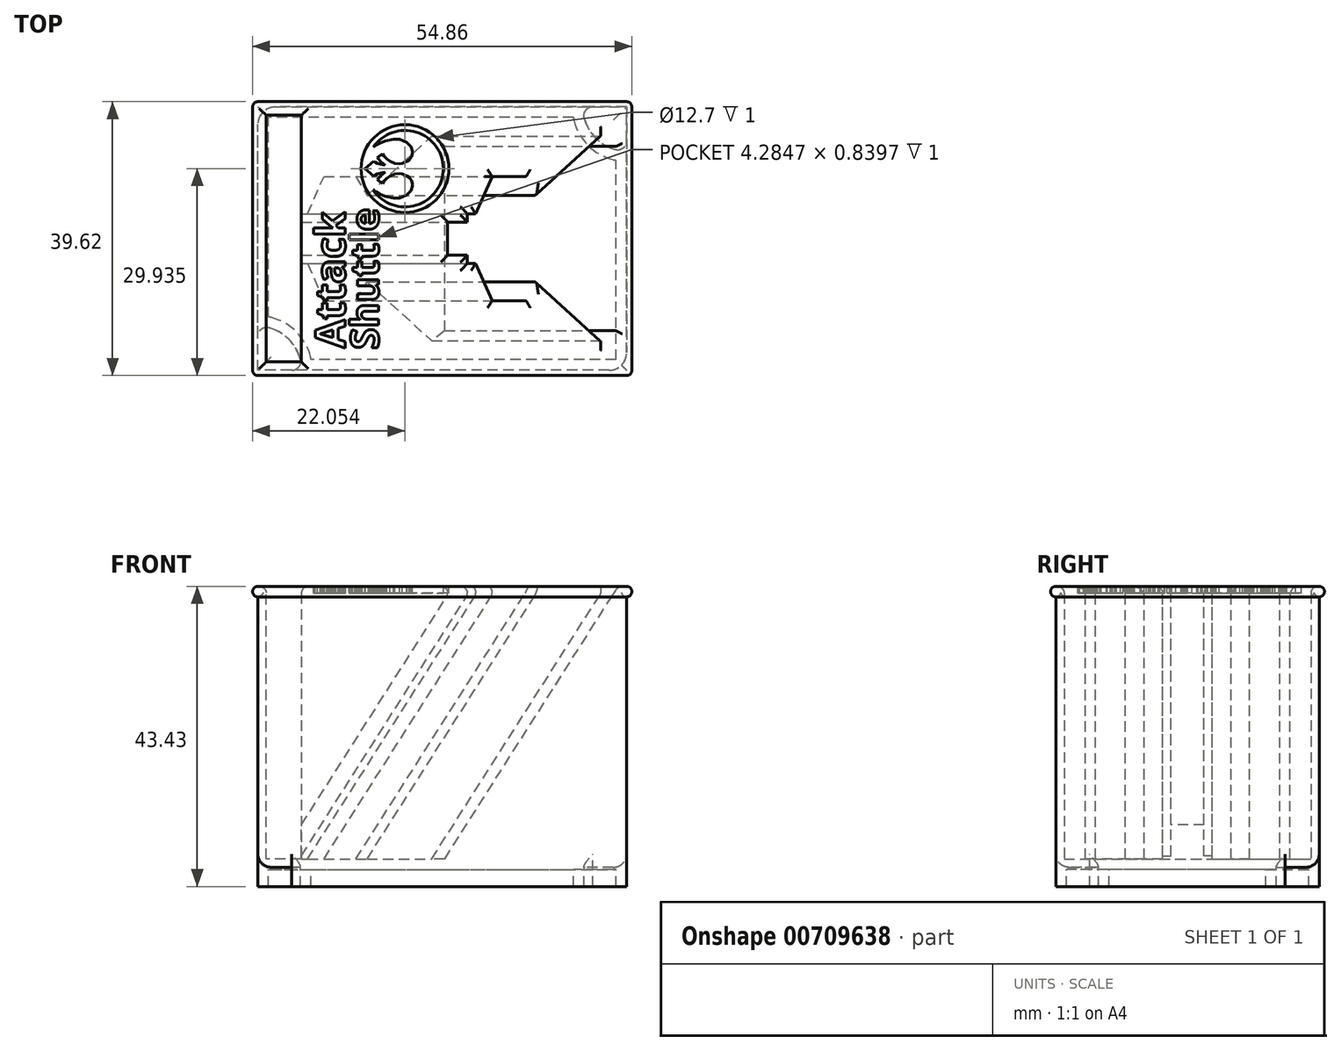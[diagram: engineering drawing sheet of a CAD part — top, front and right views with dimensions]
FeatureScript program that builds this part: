
annotation { "Feature Type Name" : "Feature", "Feature Type Description" : "" }
export const myFeature = defineFeature(function(context is Context, id is Id, definition is map)
    precondition{}
    {
        {
            var Q0;
            Q0=qCreatedBy(makeId("Front.planeOp"),FACE);
            var sketch = newSketch(context, id + "F0", { "sketchPlane" : qUnion([Q0])});
            skLineSegment(sketch, "E0.bottom", {"start": v(26.67, -20.32) * mm, "end": v(-26.67, -20.32) * mm});
            skLineSegment(sketch, "E0.top", {"start": v(26.67, 20.32) * mm, "end": v(-26.67, 20.32) * mm});
            skLineSegment(sketch, "E0.left", {"start": v(26.67, -20.32) * mm, "end": v(26.67, 20.32) * mm});
            skLineSegment(sketch, "E0.right", {"start": v(-26.67, -20.32) * mm, "end": v(-26.67, 20.32) * mm});
            skPoint(sketch, "E0.middle", {"position": v(0, 0) * mm});
            skSolve(sketch);
        }
        {
            var Q0;
            Q0=makeQuery(id+"F0.imprint","IMPRINT",FACE,{"disambiguationData":[TD([[makeQuery(id+"F0.imprint","IMPRINT",EDGE,{"derivedFrom":sQuery(id+"F0.wireOp",EDGE,"E0.bottom")}),-1.0]])]});
            extrude(context, id + "F1", {"entities" : qUnion([Q0]), "depth" : 38.1 * mm, "symmetric" : true});
        }
        {
            var Q0;
            Q0=makeQuery(id+"F1.opExtrude","SWEPT_FACE",FACE,{"disambiguationData":[OSD([sQuery(id+"F0.wireOp",EDGE,"E0.top")])]});
            shell(context, id + "F2", {"entities" : qUnion([Q0]), "thickness" : 1.2 * mm});
        }
        {
            var Q0;
            Q0=makeQuery(id+"F1.opExtrude","CAP_FACE",FACE,{"disambiguationData":[OSD([sQuery(id+"F0.wireOp",EDGE,"E0.bottom"),sQuery(id+"F0.wireOp",EDGE,"E0.top"),sQuery(id+"F0.wireOp",EDGE,"E0.left"),sQuery(id+"F0.wireOp",EDGE,"E0.right")])],"isStart":false});
            var sketch = newSketch(context, id + "F3", { "sketchPlane" : qUnion([Q0])});
            skArc(sketch, "E1", {"start": v(-26.67, 20.32) * mm, "mid": v(-27.43, 19.56) * mm, "end": v(-26.67, 18.8) * mm});
            skSolve(sketch);
        }
        {
            var Q0;
            {var subQ0=sQuery(id+"F3.wireOp",EDGE,"E1");Q0=makeQuery(id+"F3.imprint","IMPRINT",FACE,{"disambiguationData":[TD([[makeQuery(id+"F3.imprint","IMPRINT",EDGE,{"derivedFrom":subQ0}),1.0]])]});}
            var Q1;
            Q1=makeQuery(id+"F1.opExtrude","SWEPT_EDGE",EDGE,{"disambiguationData":[OSD([sQuery(id+"F0.wireOp",EDGE,"E0.top"),sQuery(id+"F0.wireOp",EDGE,"E0.right")])]});
            var Q2;
            Q2=makeQuery(id+"F1.opExtrude","CAP_EDGE",EDGE,{"disambiguationData":[OSD([sQuery(id+"F0.wireOp",EDGE,"E0.top")])],"isStart":true});
            var Q3;
            Q3=makeQuery(id+"F1.opExtrude","SWEPT_EDGE",EDGE,{"disambiguationData":[OSD([sQuery(id+"F0.wireOp",EDGE,"E0.top"),sQuery(id+"F0.wireOp",EDGE,"E0.left")])]});
            var Q4;
            Q4=makeQuery(id+"F1.opExtrude","CAP_EDGE",EDGE,{"disambiguationData":[OSD([sQuery(id+"F0.wireOp",EDGE,"E0.top")])],"isStart":false});
            sweep(context, id + "F4", {"operationType" : NewBodyOperationType.ADD, "profiles" : qUnion([Q0]), "path" : qUnion([Q1, Q2, Q3, Q4])});
        }
        {
            var Q0;
            Q0=makeQuery(id+"F1.opExtrude","SWEPT_FACE",FACE,{"disambiguationData":[OSD([sQuery(id+"F0.wireOp",EDGE,"E0.bottom")])]});
            var sketch = newSketch(context, id + "F5", { "sketchPlane" : qUnion([Q0])});
            skLineSegment(sketch, "E2.bottom", {"start": v(26.67, 19.05) * mm, "end": v(21.75, 19.05) * mm});
            skLineSegment(sketch, "E2.left", {"start": v(26.67, 19.05) * mm, "end": v(26.67, 14.13) * mm});
            skPoint(sketch, "E3.newPointA", {"position": v(20.32, 19.05) * mm});
            skArc(sketch, "E4", {"start": v(20.52, 17.46) * mm, "mid": v(22.18, 14.56) * mm, "end": v(25.08, 12.9) * mm});
            skArc(sketch, "E5.filletArc", {"start": v(21.75, 19.05) * mm, "mid": v(20.75, 18.56) * mm, "end": v(20.52, 17.46) * mm});
            skPoint(sketch, "E6.visualSharp", {"position": v(26.67, 12.7) * mm});
            skArc(sketch, "E6.filletArc", {"start": v(25.08, 12.9) * mm, "mid": v(26.18, 13.13) * mm, "end": v(26.67, 14.13) * mm});
            skArc(sketch, "E7.MirrorCS", {"start": v(-21.75, 19.05) * mm, "mid": v(-20.75, 18.56) * mm, "end": v(-20.52, 17.46) * mm});
            skArc(sketch, "E8.MirrorCS", {"start": v(-20.52, 17.46) * mm, "mid": v(-22.18, 14.56) * mm, "end": v(-25.08, 12.9) * mm});
            skArc(sketch, "E9.MirrorCS", {"start": v(-25.08, 12.9) * mm, "mid": v(-26.18, 13.13) * mm, "end": v(-26.67, 14.13) * mm});
            skLineSegment(sketch, "E10.MirrorCS", {"start": v(-26.67, 19.05) * mm, "end": v(-26.67, 14.13) * mm});
            skLineSegment(sketch, "E11.MirrorCS", {"start": v(-26.67, 19.05) * mm, "end": v(-21.75, 19.05) * mm});
            skArc(sketch, "E12.MirrorCS", {"start": v(-20.52, -17.46) * mm, "mid": v(-22.18, -14.56) * mm, "end": v(-25.08, -12.9) * mm});
            skArc(sketch, "E13.MirrorCS", {"start": v(-21.75, -19.05) * mm, "mid": v(-20.75, -18.56) * mm, "end": v(-20.52, -17.46) * mm});
            skLineSegment(sketch, "E14.MirrorCS", {"start": v(-26.67, -19.05) * mm, "end": v(-21.75, -19.05) * mm});
            skLineSegment(sketch, "E15.MirrorCS", {"start": v(-26.67, -19.05) * mm, "end": v(-26.67, -14.13) * mm});
            skArc(sketch, "E16.MirrorCS", {"start": v(-25.08, -12.9) * mm, "mid": v(-26.18, -13.13) * mm, "end": v(-26.67, -14.13) * mm});
            skArc(sketch, "E17.MirrorCS", {"start": v(21.75, -19.05) * mm, "mid": v(20.75, -18.56) * mm, "end": v(20.52, -17.46) * mm});
            skArc(sketch, "E18.MirrorCS", {"start": v(20.52, -17.46) * mm, "mid": v(22.18, -14.56) * mm, "end": v(25.08, -12.9) * mm});
            skArc(sketch, "E19.MirrorCS", {"start": v(25.08, -12.9) * mm, "mid": v(26.18, -13.13) * mm, "end": v(26.67, -14.13) * mm});
            skLineSegment(sketch, "E20.MirrorCS", {"start": v(26.67, -19.05) * mm, "end": v(26.67, -14.13) * mm});
            skLineSegment(sketch, "E21.MirrorCS", {"start": v(26.67, -19.05) * mm, "end": v(21.75, -19.05) * mm});
            skSolve(sketch);
        }
        {
            var Q0;
            Q0=makeQuery(id+"F5.imprint","IMPRINT",FACE,{"disambiguationData":[TD([[makeQuery(id+"F5.imprint","IMPRINT",EDGE,{"derivedFrom":sQuery(id+"F5.wireOp",EDGE,"E2.bottom")}),1.0]])]});
            var Q1;
            Q1=makeQuery(id+"F5.imprint","IMPRINT",FACE,{"disambiguationData":[TD([[makeQuery(id+"F5.imprint","IMPRINT",EDGE,{"derivedFrom":sQuery(id+"F5.wireOp",EDGE,"E8.MirrorCS")}),-1.0]])]});
            var Q2;
            Q2=makeQuery(id+"F5.imprint","IMPRINT",FACE,{"disambiguationData":[TD([[makeQuery(id+"F5.imprint","IMPRINT",EDGE,{"derivedFrom":sQuery(id+"F5.wireOp",EDGE,"E12.MirrorCS")}),1.0]])]});
            var Q3;
            Q3=makeQuery(id+"F5.imprint","IMPRINT",FACE,{"disambiguationData":[TD([[makeQuery(id+"F5.imprint","IMPRINT",EDGE,{"derivedFrom":sQuery(id+"F5.wireOp",EDGE,"E17.MirrorCS")}),-1.0]])]});
            extrude(context, id + "F6", {"entities" : qUnion([Q0, Q1, Q2, Q3]), "operationType" : NewBodyOperationType.ADD, "depth" : 2.8 * mm});
        }
        {
            var Q0;
            Q0=makeQuery(id+"F6.opExtrude","CAP_FACE",FACE,{"disambiguationData":[OSD([sQuery(id+"F5.wireOp",EDGE,"E2.bottom"),sQuery(id+"F5.wireOp",EDGE,"E2.left"),sQuery(id+"F5.wireOp",EDGE,"E4"),sQuery(id+"F5.wireOp",EDGE,"E5.filletArc"),sQuery(id+"F5.wireOp",EDGE,"E6.filletArc")])],"isStart":false});
            var Q1;
            Q1=makeQuery(id+"F6.opExtrude","CAP_FACE",FACE,{"disambiguationData":[OSD([sQuery(id+"F5.wireOp",EDGE,"E8.MirrorCS"),sQuery(id+"F5.wireOp",EDGE,"E9.MirrorCS"),sQuery(id+"F5.wireOp",EDGE,"E10.MirrorCS"),sQuery(id+"F5.wireOp",EDGE,"E7.MirrorCS"),sQuery(id+"F5.wireOp",EDGE,"E11.MirrorCS")])],"isStart":false});
            var Q2;
            Q2=makeQuery(id+"F6.opExtrude","CAP_FACE",FACE,{"disambiguationData":[OSD([sQuery(id+"F5.wireOp",EDGE,"E12.MirrorCS"),sQuery(id+"F5.wireOp",EDGE,"E13.MirrorCS"),sQuery(id+"F5.wireOp",EDGE,"E14.MirrorCS"),sQuery(id+"F5.wireOp",EDGE,"E15.MirrorCS"),sQuery(id+"F5.wireOp",EDGE,"E16.MirrorCS")])],"isStart":false});
            var Q3;
            Q3=makeQuery(id+"F6.opExtrude","CAP_FACE",FACE,{"disambiguationData":[OSD([sQuery(id+"F5.wireOp",EDGE,"E17.MirrorCS"),sQuery(id+"F5.wireOp",EDGE,"E18.MirrorCS"),sQuery(id+"F5.wireOp",EDGE,"E19.MirrorCS"),sQuery(id+"F5.wireOp",EDGE,"E20.MirrorCS"),sQuery(id+"F5.wireOp",EDGE,"E21.MirrorCS")])],"isStart":false});
            shell(context, id + "F7", {"entities" : qUnion([Q0, Q1, Q2, Q3]), "thickness" : 1.52 * mm});
        }
        {
            var Q0;
            Q0=makeQuery(id+"F1.opExtrude","SWEPT_EDGE",EDGE,{"disambiguationData":[OSD([sQuery(id+"F0.wireOp",EDGE,"E0.bottom"),sQuery(id+"F0.wireOp",EDGE,"E0.right")])]});
            var Q1;
            Q1=makeQuery(id+"F1.opExtrude","CAP_EDGE",EDGE,{"disambiguationData":[OSD([sQuery(id+"F0.wireOp",EDGE,"E0.bottom")])],"isStart":false});
            var Q2;
            Q2=makeQuery(id+"F1.opExtrude","SWEPT_EDGE",EDGE,{"disambiguationData":[OSD([sQuery(id+"F0.wireOp",EDGE,"E0.bottom"),sQuery(id+"F0.wireOp",EDGE,"E0.left")])]});
            var Q3;
            Q3=makeQuery(id+"F1.opExtrude","CAP_EDGE",EDGE,{"disambiguationData":[OSD([sQuery(id+"F0.wireOp",EDGE,"E0.bottom")])],"isStart":true});
            fillet(context, id + "F8", {"entities" : qUnion([Q0, Q1, Q2, Q3]), "radius" : 1.9 * mm, "tangentPropagation" : true, "allowEdgeOverflow" : false});
        }
        {
            var Q0;
            Q0=makeQuery(id+"F4.opSweep","MID_CAP_EDGE",EDGE,{"disambiguationData":[OSD([sQuery(id+"F0.wireOp",EDGE,"E0.top"),sQuery(id+"F0.wireOp",EDGE,"E0.left"),sQuery(id+"F3.wireOp",EDGE,"E1")])],"capPos":3.0});
            var Q1;
            Q1=makeQuery(id+"F4.opSweep","MID_CAP_EDGE",EDGE,{"disambiguationData":[OSD([sQuery(id+"F0.wireOp",EDGE,"E0.top"),sQuery(id+"F0.wireOp",EDGE,"E0.left"),sQuery(id+"F3.wireOp",EDGE,"E1")])],"capPos":2.0});
            var Q2;
            Q2=makeQuery(id+"F4.opSweep","MID_CAP_EDGE",EDGE,{"disambiguationData":[OSD([sQuery(id+"F0.wireOp",EDGE,"E0.top"),sQuery(id+"F0.wireOp",EDGE,"E0.right"),sQuery(id+"F3.wireOp",EDGE,"E1")])],"capPos":1.0});
            var Q3;
            Q3=makeQuery(id+"F4.opSweep","CAP_EDGE",EDGE,{"disambiguationData":[OSD([sQuery(id+"F0.wireOp",EDGE,"E0.top"),sQuery(id+"F0.wireOp",EDGE,"E0.right"),sQuery(id+"F3.wireOp",EDGE,"E1")])],"isStart":true});
            fillet(context, id + "F9", {"entities" : qUnion([Q0, Q1, Q2, Q3]), "radius" : 0.76 * mm, "tangentPropagation" : true, "allowEdgeOverflow" : false});
        }
        {
            var Q0;
            Q0=makeQuery(id+"F6.boolean.opBoolean","MERGE",EDGE,{"derivedFrom":[makeQuery(id+"F1.opExtrude","CAP_EDGE",EDGE,{"disambiguationData":[OSD([sQuery(id+"F0.wireOp",EDGE,"E0.left")])],"isStart":false}),makeQuery(id+"F6.opExtrude","SWEPT_EDGE",EDGE,{"disambiguationData":[OSD([sQuery(id+"F5.wireOp",EDGE,"E2.bottom"),sQuery(id+"F5.wireOp",EDGE,"E2.left")])]})]});
            var Q1;
            Q1=makeQuery(id+"F6.boolean.opBoolean","MERGE",EDGE,{"derivedFrom":[makeQuery(id+"F1.opExtrude","CAP_EDGE",EDGE,{"disambiguationData":[OSD([sQuery(id+"F0.wireOp",EDGE,"E0.left")])],"isStart":true}),makeQuery(id+"F6.opExtrude","SWEPT_EDGE",EDGE,{"disambiguationData":[OSD([sQuery(id+"F5.wireOp",EDGE,"E20.MirrorCS"),sQuery(id+"F5.wireOp",EDGE,"E21.MirrorCS")])]})]});
            var Q2;
            Q2=makeQuery(id+"F6.boolean.opBoolean","MERGE",EDGE,{"derivedFrom":[makeQuery(id+"F1.opExtrude","CAP_EDGE",EDGE,{"disambiguationData":[OSD([sQuery(id+"F0.wireOp",EDGE,"E0.right")])],"isStart":false}),makeQuery(id+"F6.opExtrude","SWEPT_EDGE",EDGE,{"disambiguationData":[OSD([sQuery(id+"F5.wireOp",EDGE,"E10.MirrorCS"),sQuery(id+"F5.wireOp",EDGE,"E11.MirrorCS")])]})]});
            var Q3;
            Q3=makeQuery(id+"F6.boolean.opBoolean","MERGE",EDGE,{"derivedFrom":[makeQuery(id+"F1.opExtrude","CAP_EDGE",EDGE,{"disambiguationData":[OSD([sQuery(id+"F0.wireOp",EDGE,"E0.right")])],"isStart":true}),makeQuery(id+"F6.opExtrude","SWEPT_EDGE",EDGE,{"disambiguationData":[OSD([sQuery(id+"F5.wireOp",EDGE,"E14.MirrorCS"),sQuery(id+"F5.wireOp",EDGE,"E15.MirrorCS")])]})]});
            fillet(context, id + "F10", {"entities" : qUnion([Q0, Q1, Q2, Q3]), "radius" : 2.54 * mm, "tangentPropagation" : true, "allowEdgeOverflow" : false});
        }
        {
            var Q0;
            Q0=makeQuery(id+"F2.opShell","OFFSET_EDGE",EDGE,{"disambiguationData":[OSD([sQuery(id+"F0.wireOp",EDGE,"E0.top"),sQuery(id+"F0.wireOp",EDGE,"E0.left")])]});
            cPlane(context, id + "F11", {"entities" : qUnion([Q0]), "cplaneType" : CPlaneType.LINE_ANGLE, "offset" : 25 * mm, "angle" : 32.5 * degree, "width" : 150 * mm, "height" : 150 * mm});
        }
        {
            var Q0;
            Q0=qCreatedBy(id+"F11.planeOp",FACE);
            var sketch = newSketch(context, id + "F12", { "sketchPlane" : qUnion([Q0])});
            skLineSegment(sketch, "E22", {"start": v(58.48, 35.77) * mm, "end": v(58.48, -3.33) * mm});
            skLineSegment(sketch, "E23", {"start": v(58.48, -3.33) * mm, "end": v(83.38, -3.33) * mm});
            skLineSegment(sketch, "E24", {"start": v(83.38, -3.33) * mm, "end": v(58.48, 35.77) * mm});
            skLineSegment(sketch, "E25", {"start": v(10.79, -61.22) * mm, "end": v(10.79, -63.22) * mm});
            skLineSegment(sketch, "E26", {"start": v(10.79, -63.22) * mm, "end": v(16.55, -63.22) * mm});
            skLineSegment(sketch, "E27", {"start": v(7.55, -61.22) * mm, "end": v(5.55, -57.22) * mm});
            skLineSegment(sketch, "E28", {"start": v(2.55, -57.22) * mm, "end": v(5.55, -57.22) * mm});
            skLineSegment(sketch, "E29", {"start": v(16.55, -63.22) * mm, "end": v(16.55, -66.22) * mm});
            skLineSegment(sketch, "E30", {"start": v(7.55, -61.22) * mm, "end": v(7.55, -60.22) * mm});
            skPoint(sketch, "E31", {"position": v(15.68, -51.42) * mm});
            skPoint(sketch, "E32", {"position": v(17.27, -52.89) * mm});
            skLineSegment(sketch, "E33", {"start": v(10.79, -61.22) * mm, "end": v(17.27, -52.89) * mm});
            skLineSegment(sketch, "E34", {"start": v(7.55, -60.22) * mm, "end": v(15.68, -51.42) * mm});
            skLineSegment(sketch, "E35", {"start": v(17.27, -52.89) * mm, "end": v(15.68, -51.42) * mm});
            skLineSegment(sketch, "E36", {"start": v(-2.85, -66.22) * mm, "end": v(-2.85, -63.82) * mm});
            skLineSegment(sketch, "E37", {"start": v(-2.85, -63.82) * mm, "end": v(-0.45, -63.82) * mm});
            skLineSegment(sketch, "E38", {"start": v(-0.45, -63.82) * mm, "end": v(-0.45, -62.62) * mm});
            skLineSegment(sketch, "E39", {"start": v(-0.45, -62.62) * mm, "end": v(0.55, -62.62) * mm});
            skLineSegment(sketch, "E40", {"start": v(0.55, -62.62) * mm, "end": v(2.55, -57.22) * mm});
            skLineSegment(sketch, "E41.MirrorCS", {"start": v(17.27, -79.55) * mm, "end": v(15.68, -81.01) * mm});
            skLineSegment(sketch, "E42.MirrorCS", {"start": v(-0.45, -69.82) * mm, "end": v(0.55, -69.82) * mm});
            skLineSegment(sketch, "E43.MirrorCS", {"start": v(-0.45, -68.62) * mm, "end": v(-0.45, -69.82) * mm});
            skLineSegment(sketch, "E44.MirrorCS", {"start": v(7.55, -71.22) * mm, "end": v(7.55, -72.22) * mm});
            skLineSegment(sketch, "E45.MirrorCS", {"start": v(10.79, -71.22) * mm, "end": v(10.79, -69.22) * mm});
            skLineSegment(sketch, "E46.MirrorCS", {"start": v(-2.85, -68.62) * mm, "end": v(-0.45, -68.62) * mm});
            skLineSegment(sketch, "E47.MirrorCS", {"start": v(10.79, -69.22) * mm, "end": v(16.55, -69.22) * mm});
            skLineSegment(sketch, "E48.MirrorCS", {"start": v(7.55, -72.22) * mm, "end": v(15.68, -81.01) * mm});
            skLineSegment(sketch, "E49.MirrorCS", {"start": v(16.55, -69.22) * mm, "end": v(16.55, -66.22) * mm});
            skLineSegment(sketch, "E50.MirrorCS", {"start": v(0.55, -69.82) * mm, "end": v(2.55, -75.22) * mm});
            skLineSegment(sketch, "E51.MirrorCS", {"start": v(10.79, -71.22) * mm, "end": v(17.27, -79.55) * mm});
            skLineSegment(sketch, "E52.MirrorCS", {"start": v(2.55, -75.22) * mm, "end": v(5.55, -75.22) * mm});
            skLineSegment(sketch, "E53.MirrorCS", {"start": v(7.55, -71.22) * mm, "end": v(5.55, -75.22) * mm});
            skLineSegment(sketch, "E54.MirrorCS", {"start": v(-2.85, -66.22) * mm, "end": v(-2.85, -68.62) * mm});
            skPoint(sketch, "E55.MirrorP", {"position": v(15.68, -81.01) * mm});
            skPoint(sketch, "E56.MirrorP", {"position": v(17.27, -79.55) * mm});
            skLineSegment(sketch, "E57", {"start": v(17.27, -81.01) * mm, "end": v(17.27, -51.42) * mm, "construction": true});
            skLineSegment(sketch, "E58", {"start": v(17.27, -51.42) * mm, "end": v(-2.85, -51.42) * mm, "construction": true});
            skLineSegment(sketch, "E59", {"start": v(17.27, -81.01) * mm, "end": v(-2.85, -81.01) * mm, "construction": true});
            skLineSegment(sketch, "E60", {"start": v(16.55, -66.22) * mm, "end": v(17.27, -66.22) * mm, "construction": true});
            skLineSegment(sketch, "E61", {"start": v(4.08, 5) * mm, "end": v(4.08, 3) * mm});
            skLineSegment(sketch, "E62", {"start": v(4.08, 3) * mm, "end": v(9.84, 3) * mm});
            skLineSegment(sketch, "E63", {"start": v(9.84, 3) * mm, "end": v(9.84, 0) * mm});
            skPoint(sketch, "E64", {"position": v(8.98, 14.8) * mm});
            skPoint(sketch, "E65", {"position": v(10.57, 13.33) * mm});
            skLineSegment(sketch, "E66", {"start": v(4.08, 5) * mm, "end": v(10.57, 13.33) * mm});
            skLineSegment(sketch, "E67", {"start": v(10.57, 13.33) * mm, "end": v(8.98, 14.8) * mm});
            skLineSegment(sketch, "E68", {"start": v(-9.56, 0) * mm, "end": v(-9.56, 2.4) * mm});
            skLineSegment(sketch, "E69", {"start": v(-9.56, 2.4) * mm, "end": v(-7.16, 2.4) * mm});
            skLineSegment(sketch, "E70", {"start": v(-7.16, 2.4) * mm, "end": v(-7.16, 3.6) * mm});
            skLineSegment(sketch, "E71", {"start": v(-7.16, 3.6) * mm, "end": v(-6.16, 3.6) * mm});
            skLineSegment(sketch, "E72", {"start": v(-6.16, 3.6) * mm, "end": v(-4.16, 9) * mm});
            skLineSegment(sketch, "E73.MirrorCS", {"start": v(10.57, -13.33) * mm, "end": v(8.98, -14.8) * mm});
            skLineSegment(sketch, "E74.MirrorCS", {"start": v(-7.16, -3.6) * mm, "end": v(-6.16, -3.6) * mm});
            skLineSegment(sketch, "E75.MirrorCS", {"start": v(-7.16, -2.4) * mm, "end": v(-7.16, -3.6) * mm});
            skLineSegment(sketch, "E76.MirrorCS", {"start": v(4.08, -5) * mm, "end": v(4.08, -3) * mm});
            skLineSegment(sketch, "E77.MirrorCS", {"start": v(-9.56, -2.4) * mm, "end": v(-7.16, -2.4) * mm});
            skLineSegment(sketch, "E78.MirrorCS", {"start": v(4.08, -3) * mm, "end": v(9.84, -3) * mm});
            skLineSegment(sketch, "E79.MirrorCS", {"start": v(1.1, -6.28) * mm, "end": v(8.98, -14.8) * mm});
            skLineSegment(sketch, "E80.MirrorCS", {"start": v(9.84, -3) * mm, "end": v(9.84, 0) * mm});
            skLineSegment(sketch, "E81.MirrorCS", {"start": v(-6.16, -3.6) * mm, "end": v(-4.16, -9) * mm});
            skLineSegment(sketch, "E82.MirrorCS", {"start": v(4.08, -5) * mm, "end": v(10.57, -13.33) * mm});
            skLineSegment(sketch, "E83.MirrorCS", {"start": v(-9.56, 0) * mm, "end": v(-9.56, -2.4) * mm});
            skPoint(sketch, "E84.MirrorP", {"position": v(8.98, -14.8) * mm});
            skPoint(sketch, "E85.MirrorP", {"position": v(10.57, -13.33) * mm});
            skLineSegment(sketch, "E86", {"start": v(-4.16, -9) * mm, "end": v(-0.26, -9) * mm});
            skLineSegment(sketch, "E87", {"start": v(-0.26, -9) * mm, "end": v(1.1, -6.28) * mm});
            skLineSegment(sketch, "E88.MirrorCS", {"start": v(1.1, 6.28) * mm, "end": v(8.98, 14.8) * mm});
            skLineSegment(sketch, "E89.MirrorCS", {"start": v(-0.26, 9) * mm, "end": v(1.1, 6.28) * mm});
            skLineSegment(sketch, "E90.MirrorCS", {"start": v(-4.16, 9) * mm, "end": v(-0.26, 9) * mm});
            skLineSegment(sketch, "E91", {"start": v(10.57, -14.8) * mm, "end": v(10.57, 14.8) * mm, "construction": true});
            skLineSegment(sketch, "E92.0", {"start": v(10.57, -17.85) * mm, "end": v(10.57, 17.85) * mm});
            skSolve(sketch);
        }
        {
            var Q0;
            Q0=makeQuery(id+"F2.opShell","OFFSET_FACE",FACE,{"disambiguationData":[OSD([sQuery(id+"F0.wireOp",EDGE,"E0.bottom")])]});
            var sketch = newSketch(context, id + "F13", { "sketchPlane" : qUnion([Q0])});
            skLineSegment(sketch, "E93.bottom", {"start": v(-25.47, -17.85) * mm, "end": v(-25.47, 17.85) * mm});
            skLineSegment(sketch, "E93.top", {"start": v(-20.37, -17.85) * mm, "end": v(-20.37, 17.85) * mm});
            skPoint(sketch, "E93.middle", {"position": v(-22.6, 0) * mm});
            skLineSegment(sketch, "E94.0", {"start": v(25.47, 17.85) * mm, "end": v(-20.37, 17.85) * mm});
            skLineSegment(sketch, "E94.1", {"start": v(25.47, -17.85) * mm, "end": v(-20.37, -17.85) * mm});
            skLineSegment(sketch, "E94.2", {"start": v(25.15, -17.53) * mm, "end": v(25.15, 17.53) * mm});
            skPoint(sketch, "E95.orphan", {"position": v(-25.47, -17.85) * mm});
            skPoint(sketch, "E96.orphan", {"position": v(-25.47, 17.85) * mm});
            skSolve(sketch);
        }
        {
            var Q0;
            {var subQ0=sQuery(id+"F13.wireOp",EDGE,"E93.bottom");var subQ1=sQuery(id+"F0.wireOp",EDGE,"E0.bottom");var subQ2=makeQuery(id+"F2.opShell","OFFSET_EDGE",EDGE,{"disambiguationData":[OSD([subQ1]),TDD([makeQuery(id+"F1.opExtrude","CAP_EDGE",EDGE,{"disambiguationData":[OSD([subQ1])],"isStart":true})])]});var subQ3=makeQuery(id+"F13.imprint","INTERSECT",VERTEX,{"derivedFrom":[subQ2,subQ0]});Q0=makeQuery(id+"F13.imprint","IMPRINT",FACE,{"disambiguationData":[TD([[makeQuery(id+"F13.imprint","IMPRINT",EDGE,{"disambiguationData":[TD([[subQ3,1.0]])],"derivedFrom":subQ0}),-1.0]])]});}
            var Q1;
            {var subQ4=sQuery(id+"F13.wireOp",EDGE,"E93.left");Q1=makeQuery(id+"F13.imprint","IMPRINT",FACE,{"disambiguationData":[TD([[makeQuery(id+"F13.imprint","IMPRINT",EDGE,{"derivedFrom":subQ4}),1.0]])]});}
            var Q2;
            {var subQ4=sQuery(id+"F13.wireOp",EDGE,"E93.right");Q2=makeQuery(id+"F13.imprint","IMPRINT",FACE,{"disambiguationData":[TD([[makeQuery(id+"F13.imprint","IMPRINT",EDGE,{"derivedFrom":subQ4}),-1.0]])]});}
            var Q3;
            {var subQ0=sQuery(id+"F0.wireOp",EDGE,"E0.right");var subQ1=sQuery(id+"F0.wireOp",EDGE,"E0.top");Q3=makeQuery(id+"F2.opShell","OFFSET_VERTEX",VERTEX,{"disambiguationData":[OSD([subQ1,subQ0]),TDD([makeQuery(id+"F1.opExtrude","CAP_VERTEX",VERTEX,{"disambiguationData":[OSD([subQ1,subQ0])],"isStart":true})])]});}
            extrude(context, id + "F14", {"entities" : qUnion([Q0, Q1, Q2]), "operationType" : NewBodyOperationType.REMOVE, "endBound" : BoundingType.UP_TO_VERTEX, "depth" : 25 * mm, "endBoundEntityVertex" : qUnion([Q3]), "offsetDistance" : 25 * mm});
        }
        {
            var Q0;
            {var subQ0=sQuery(id+"F13.wireOp",EDGE,"E94.0");Q0=makeQuery(id+"F13.imprint","IMPRINT",FACE,{"disambiguationData":[TD([[makeQuery(id+"F13.imprint","IMPRINT",EDGE,{"derivedFrom":subQ0}),1.0]])]});}
            var Q1;
            {var subQ0=sQuery(id+"F0.wireOp",EDGE,"E0.right");var subQ1=sQuery(id+"F0.wireOp",EDGE,"E0.top");Q1=makeQuery(id+"F2.opShell","OFFSET_VERTEX",VERTEX,{"disambiguationData":[OSD([subQ1,subQ0]),TDD([makeQuery(id+"F1.opExtrude","CAP_VERTEX",VERTEX,{"disambiguationData":[OSD([subQ1,subQ0])],"isStart":true})])]});}
            extrude(context, id + "F15", {"entities" : qUnion([Q0]), "operationType" : NewBodyOperationType.ADD, "endBound" : BoundingType.UP_TO_VERTEX, "depth" : 36.44 * mm, "endBoundEntityVertex" : qUnion([Q1]), "offsetDistance" : 25 * mm});
        }
        {
            var Q0;
            Q0=qSketchRegion(id+"F12",true);
            var Q1;
            Q1=makeQuery(id+"F14.boolean.opBoolean","MERGE",FACE,{"derivedFrom":[makeQuery(id+"F2.opShell","OFFSET_FACE",FACE,{"disambiguationData":[OSD([sQuery(id+"F0.wireOp",EDGE,"E0.bottom")])]})],"fromTools":[makeQuery(id+"F14.opExtrude","CAP_FACE",FACE,{"disambiguationData":[OSD([sQuery(id+"F13.wireOp",EDGE,"E93.bottom"),sQuery(id+"F13.wireOp",EDGE,"E93.top"),sQuery(id+"F13.wireOp",EDGE,"E93.left"),sQuery(id+"F13.wireOp",EDGE,"E93.right")])],"isStart":true})]});
            extrude(context, id + "F16", {"entities" : qUnion([Q0]), "operationType" : NewBodyOperationType.REMOVE, "endBound" : BoundingType.UP_TO_SURFACE, "oppositeDirection" : true, "depth" : 25 * mm, "endBoundEntityFace" : qUnion([Q1]), "offsetDistance" : 25 * mm});
        }
        {
            var Q0;
            Q0=makeQuery(id+"F15.opExtrude","CAP_FACE",FACE,{"disambiguationData":[OSD([sQuery(id+"F0.wireOp",EDGE,"E0.bottom"),sQuery(id+"F0.wireOp",EDGE,"E0.left"),sQuery(id+"F0.wireOp",EDGE,"E0.right"),sQuery(id+"F13.wireOp",EDGE,"E93.bottom"),sQuery(id+"F13.wireOp",EDGE,"E93.top"),sQuery(id+"F13.wireOp",EDGE,"E93.left"),sQuery(id+"F13.wireOp",EDGE,"E93.right"),sQuery(id+"F13.wireOp",EDGE,"E94.0"),sQuery(id+"F13.wireOp",EDGE,"E94.1")])],"isStart":false});
            fillet(context, id + "F17", {"entities" : qUnion([Q0]), "radius" : 1 * mm, "tangentPropagation" : true, "allowEdgeOverflow" : false});
        }
        {
            var Q0;
            Q0=makeQuery(id+"F15.opExtrude","CAP_FACE",FACE,{"disambiguationData":[OSD([sQuery(id+"F0.wireOp",EDGE,"E0.bottom"),sQuery(id+"F0.wireOp",EDGE,"E0.left"),sQuery(id+"F13.wireOp",EDGE,"E93.top"),sQuery(id+"F13.wireOp",EDGE,"E94.0"),sQuery(id+"F13.wireOp",EDGE,"E94.1")])],"isStart":false});
            var sketch = newSketch(context, id + "F18", { "sketchPlane" : qUnion([Q0])});
            skLineSegment(sketch, "E97", {"start": v(-9.93, 11.22) * mm, "end": v(-11.18, 10.13) * mm});
            skLineSegment(sketch, "E98", {"start": v(-9.38, 11.72) * mm, "end": v(-8.67, 12.27) * mm});
            skLineSegment(sketch, "E99", {"start": v(-8.67, 12.27) * mm, "end": v(-8.44, 11.97) * mm});
            skLineSegment(sketch, "E100", {"start": v(-8.44, 11.97) * mm, "end": v(-7.99, 11.52) * mm});
            skLineSegment(sketch, "E101", {"start": v(-7.99, 11.52) * mm, "end": v(-7.58, 11.2) * mm});
            skLineSegment(sketch, "E102", {"start": v(-7.58, 11.2) * mm, "end": v(-6.88, 10.9) * mm});
            skLineSegment(sketch, "E103", {"start": v(-6.88, 10.9) * mm, "end": v(-6.13, 10.82) * mm});
            skLineSegment(sketch, "E104", {"start": v(-6.13, 10.82) * mm, "end": v(-5.76, 10.89) * mm});
            skLineSegment(sketch, "E105", {"start": v(-5.76, 10.89) * mm, "end": v(-5.07, 11.2) * mm});
            skLineSegment(sketch, "E106", {"start": v(-5.07, 11.2) * mm, "end": v(-4.75, 11.4) * mm});
            skLineSegment(sketch, "E107", {"start": v(-4.75, 11.4) * mm, "end": v(-4.46, 11.82) * mm});
            skLineSegment(sketch, "E108", {"start": v(-4.46, 11.82) * mm, "end": v(-4.31, 12.31) * mm});
            skLineSegment(sketch, "E109", {"start": v(-4.31, 12.31) * mm, "end": v(-4.31, 12.69) * mm});
            skLineSegment(sketch, "E110", {"start": v(-4.31, 12.69) * mm, "end": v(-4.5, 13.3) * mm});
            skLineSegment(sketch, "E111", {"start": v(-4.5, 13.3) * mm, "end": v(-5.12, 13.95) * mm});
            skLineSegment(sketch, "E112", {"start": v(-5.12, 13.95) * mm, "end": v(-6.15, 14.4) * mm});
            skLineSegment(sketch, "E113", {"start": v(-6.15, 14.4) * mm, "end": v(-7.03, 14.4) * mm});
            skLineSegment(sketch, "E114", {"start": v(-7.03, 14.4) * mm, "end": v(-8.28, 14.11) * mm});
            skLineSegment(sketch, "E115", {"start": v(-8.28, 14.11) * mm, "end": v(-8.99, 13.81) * mm});
            skLineSegment(sketch, "E116", {"start": v(-8.99, 13.81) * mm, "end": v(-9.54, 13.52) * mm});
            skLineSegment(sketch, "E117", {"start": v(-9.54, 13.52) * mm, "end": v(-9.96, 13.23) * mm});
            skLineSegment(sketch, "E118", {"start": v(-9.38, 11.72) * mm, "end": v(-9.22, 11.5) * mm});
            skLineSegment(sketch, "E119", {"start": v(-9.22, 11.5) * mm, "end": v(-8.86, 11.14) * mm});
            skLineSegment(sketch, "E120", {"start": v(-8.86, 11.14) * mm, "end": v(-8.6, 10.87) * mm});
            skLineSegment(sketch, "E121", {"start": v(-8.6, 10.87) * mm, "end": v(-8.28, 10.65) * mm});
            skLineSegment(sketch, "E122", {"start": v(-8.28, 10.65) * mm, "end": v(-8.91, 10.75) * mm});
            skLineSegment(sketch, "E123", {"start": v(-8.91, 10.75) * mm, "end": v(-9.38, 10.9) * mm});
            skLineSegment(sketch, "E124", {"start": v(-9.38, 10.9) * mm, "end": v(-9.72, 11.05) * mm});
            skLineSegment(sketch, "E125", {"start": v(-9.72, 11.05) * mm, "end": v(-9.93, 11.22) * mm});
            skPoint(sketch, "E126.start.orphan", {"position": v(-11.73, 10.13) * mm});
            skLineSegment(sketch, "E127.MirrorCS", {"start": v(-4.75, 8.85) * mm, "end": v(-4.46, 8.43) * mm});
            skLineSegment(sketch, "E128.MirrorCS", {"start": v(-8.99, 6.44) * mm, "end": v(-9.54, 6.73) * mm});
            skLineSegment(sketch, "E129.MirrorCS", {"start": v(-5.07, 9.06) * mm, "end": v(-4.75, 8.85) * mm});
            skLineSegment(sketch, "E130.MirrorCS", {"start": v(-6.15, 5.85) * mm, "end": v(-7.03, 5.85) * mm});
            skLineSegment(sketch, "E131.MirrorCS", {"start": v(-8.28, 9.6) * mm, "end": v(-8.91, 9.5) * mm});
            skLineSegment(sketch, "E132.MirrorCS", {"start": v(-8.44, 8.28) * mm, "end": v(-7.99, 8.73) * mm});
            skLineSegment(sketch, "E133.MirrorCS", {"start": v(-8.91, 9.5) * mm, "end": v(-9.38, 9.34) * mm});
            skLineSegment(sketch, "E134.MirrorCS", {"start": v(-9.38, 9.34) * mm, "end": v(-9.72, 9.2) * mm});
            skLineSegment(sketch, "E135.MirrorCS", {"start": v(-8.6, 9.38) * mm, "end": v(-8.28, 9.6) * mm});
            skLineSegment(sketch, "E136.MirrorCS", {"start": v(-4.31, 7.56) * mm, "end": v(-4.5, 6.95) * mm});
            skLineSegment(sketch, "E137.MirrorCS", {"start": v(-4.5, 6.95) * mm, "end": v(-5.12, 6.3) * mm});
            skLineSegment(sketch, "E138.MirrorCS", {"start": v(-9.54, 6.73) * mm, "end": v(-9.96, 7.02) * mm});
            skLineSegment(sketch, "E139.MirrorCS", {"start": v(-8.28, 6.14) * mm, "end": v(-8.99, 6.44) * mm});
            skLineSegment(sketch, "E140.MirrorCS", {"start": v(-9.22, 8.74) * mm, "end": v(-8.86, 9.1) * mm});
            skLineSegment(sketch, "E141.MirrorCS", {"start": v(-7.99, 8.73) * mm, "end": v(-7.58, 9.05) * mm});
            skLineSegment(sketch, "E142.MirrorCS", {"start": v(-4.46, 8.43) * mm, "end": v(-4.31, 7.94) * mm});
            skLineSegment(sketch, "E143.MirrorCS", {"start": v(-8.67, 7.98) * mm, "end": v(-8.44, 8.28) * mm});
            skLineSegment(sketch, "E144.MirrorCS", {"start": v(-9.38, 8.53) * mm, "end": v(-9.22, 8.74) * mm});
            skLineSegment(sketch, "E145.MirrorCS", {"start": v(-5.76, 9.36) * mm, "end": v(-5.07, 9.06) * mm});
            skLineSegment(sketch, "E146.MirrorCS", {"start": v(-9.38, 8.53) * mm, "end": v(-8.67, 7.98) * mm});
            skLineSegment(sketch, "E147.MirrorCS", {"start": v(-6.13, 9.43) * mm, "end": v(-5.76, 9.36) * mm});
            skLineSegment(sketch, "E148.MirrorCS", {"start": v(-7.58, 9.05) * mm, "end": v(-6.88, 9.35) * mm});
            skLineSegment(sketch, "E149.MirrorCS", {"start": v(-6.88, 9.35) * mm, "end": v(-6.13, 9.43) * mm});
            skLineSegment(sketch, "E150.MirrorCS", {"start": v(-8.86, 9.1) * mm, "end": v(-8.6, 9.38) * mm});
            skLineSegment(sketch, "E151.MirrorCS", {"start": v(-9.72, 9.2) * mm, "end": v(-9.93, 9.03) * mm});
            skLineSegment(sketch, "E152.MirrorCS", {"start": v(-4.31, 7.94) * mm, "end": v(-4.31, 7.56) * mm});
            skLineSegment(sketch, "E153.MirrorCS", {"start": v(-7.03, 5.85) * mm, "end": v(-8.28, 6.14) * mm});
            skLineSegment(sketch, "E154.MirrorCS", {"start": v(-9.93, 9.03) * mm, "end": v(-11.18, 10.13) * mm});
            skLineSegment(sketch, "E155.MirrorCS", {"start": v(-5.12, 6.3) * mm, "end": v(-6.15, 5.85) * mm});
            skCircle(sketch, "E156.MirrorC", {"center": v(-5.38, 10.13) * mm, "radius": 6.35 * mm});
            skArc(sketch, "E157", {"start": v(-9.96, 7.02) * mm, "mid": v(0.16, 10.13) * mm, "end": v(-9.96, 13.23) * mm});
            skText(sketch, "E158", { "text": "Attack", "fontName": "NotoSans-Bold.ttf"});
            skPoint(sketch, "E159.0", {"position": v(-19.37, -16.85) * mm});
            skLineSegment(sketch, "E160", {"start": v(-19.37, -15.85) * mm, "end": v(-18.37, -15.85) * mm, "construction": true});
            skText(sketch, "E161", { "text": "Shuttle", "fontName": "NotoSans-Bold.ttf"});
            skLineSegment(sketch, "E162", {"start": v(-9.2, -16.85) * mm, "end": v(-9.2, -16.05) * mm, "construction": true});
            skLineSegment(sketch, "E163", {"start": v(-13.25, -5.77) * mm, "end": v(-14.05, -5.77) * mm, "construction": true});
            const initialGuessF18  = {"E158": [-0.01405, -0.01585, 0, 1, 0.00432], "E161": [-0.0092, -0.01605, 0, 1, 0.00406]};
            skSetInitialGuess(sketch, initialGuessF18);
            skSolve(sketch);
        }
        {
            var Q0;
            Q0=makeQuery(id+"F18.imprint","IMPRINT",FACE,{"disambiguationData":[TD([[makeQuery(id+"F18.imprint","IMPRINT",EDGE,{"derivedFrom":sQuery(id+"F18.wireOp",EDGE,"E158.sketch_text.stroke-12")}),-1.0]])]});
            var Q1;
            Q1=makeQuery(id+"F18.imprint","IMPRINT",FACE,{"disambiguationData":[TD([[makeQuery(id+"F18.imprint","IMPRINT",EDGE,{"derivedFrom":sQuery(id+"F18.wireOp",EDGE,"E158.sketch_text.stroke-30")}),-1.0]])]});
            var Q2;
            Q2=makeQuery(id+"F18.imprint","IMPRINT",FACE,{"disambiguationData":[TD([[makeQuery(id+"F18.imprint","IMPRINT",EDGE,{"derivedFrom":sQuery(id+"F18.wireOp",EDGE,"E158.sketch_text.stroke-73")}),-1.0]])]});
            var Q3;
            Q3=makeQuery(id+"F18.imprint","IMPRINT",FACE,{"disambiguationData":[TD([[makeQuery(id+"F18.imprint","IMPRINT",EDGE,{"derivedFrom":sQuery(id+"F18.wireOp",EDGE,"E158.sketch_text.stroke-87")}),-1.0]])]});
            var Q4;
            Q4=makeQuery(id+"F18.imprint","IMPRINT",FACE,{"disambiguationData":[TD([[makeQuery(id+"F18.imprint","IMPRINT",EDGE,{"derivedFrom":sQuery(id+"F18.wireOp",EDGE,"E161.sketch_text.stroke-0")}),-1.0]])]});
            var Q5;
            Q5=makeQuery(id+"F18.imprint","IMPRINT",FACE,{"disambiguationData":[TD([[makeQuery(id+"F18.imprint","IMPRINT",EDGE,{"derivedFrom":sQuery(id+"F18.wireOp",EDGE,"E161.sketch_text.stroke-28")}),-1.0]])]});
            var Q6;
            Q6=makeQuery(id+"F18.imprint","IMPRINT",FACE,{"disambiguationData":[TD([[makeQuery(id+"F18.imprint","IMPRINT",EDGE,{"derivedFrom":sQuery(id+"F18.wireOp",EDGE,"E161.sketch_text.stroke-45")}),-1.0]])]});
            var Q7;
            Q7=makeQuery(id+"F18.imprint","IMPRINT",FACE,{"disambiguationData":[TD([[makeQuery(id+"F18.imprint","IMPRINT",EDGE,{"derivedFrom":sQuery(id+"F18.wireOp",EDGE,"E161.sketch_text.stroke-62")}),-1.0]])]});
            var Q8;
            Q8=makeQuery(id+"F18.imprint","IMPRINT",FACE,{"disambiguationData":[TD([[makeQuery(id+"F18.imprint","IMPRINT",EDGE,{"derivedFrom":sQuery(id+"F18.wireOp",EDGE,"E161.sketch_text.stroke-80")}),-1.0]])]});
            var Q9;
            Q9=makeQuery(id+"F18.imprint","IMPRINT",FACE,{"disambiguationData":[TD([[makeQuery(id+"F18.imprint","IMPRINT",EDGE,{"derivedFrom":sQuery(id+"F18.wireOp",EDGE,"E161.sketch_text.stroke-98")}),-1.0]])]});
            var Q10;
            Q10=makeQuery(id+"F18.imprint","IMPRINT",FACE,{"disambiguationData":[TD([[makeQuery(id+"F18.imprint","IMPRINT",EDGE,{"derivedFrom":sQuery(id+"F18.wireOp",EDGE,"E158.sketch_text.stroke-0")}),-1.0]])]});
            var Q11;
            Q11=makeQuery(id+"F18.imprint","IMPRINT",FACE,{"disambiguationData":[TD([[makeQuery(id+"F18.imprint","IMPRINT",EDGE,{"derivedFrom":sQuery(id+"F18.wireOp",EDGE,"E158.sketch_text.stroke-48")}),-1.0]])]});
            var Q12;
            Q12=makeQuery(id+"F18.imprint","IMPRINT",FACE,{"disambiguationData":[TD([[makeQuery(id+"F18.imprint","IMPRINT",EDGE,{"derivedFrom":sQuery(id+"F18.wireOp",EDGE,"E161.sketch_text.stroke-102")}),-1.0]])]});
            var Q13;
            Q13=makeQuery(id+"F18.imprint","IMPRINT",FACE,{"disambiguationData":[TD([[makeQuery(id+"F18.imprint","IMPRINT",EDGE,{"derivedFrom":sQuery(id+"F18.wireOp",EDGE,"E97")}),-1.0]])]});
            extrude(context, id + "F19", {"entities" : qUnion([Q0, Q1, Q2, Q3, Q4, Q5, Q6, Q7, Q8, Q9, Q10, Q11, Q12, Q13]), "operationType" : NewBodyOperationType.REMOVE, "oppositeDirection" : true, "depth" : 1 * mm, "offsetDistance" : 25 * mm});
        }
    });
